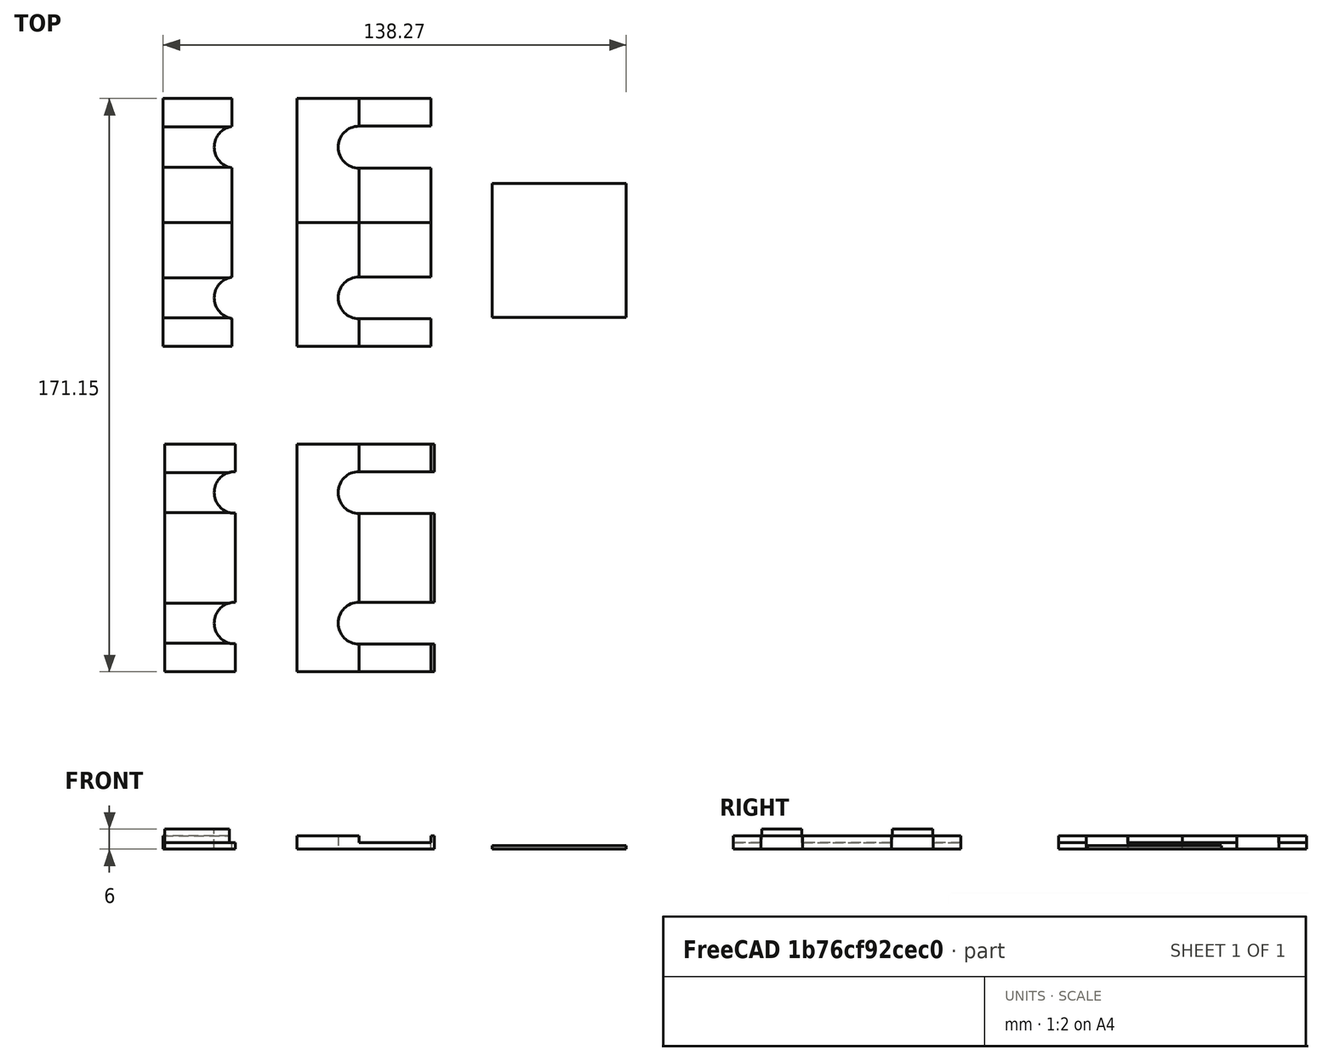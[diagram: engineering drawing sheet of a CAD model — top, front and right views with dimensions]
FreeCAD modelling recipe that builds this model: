
FCSTD DOCUMENT  (FreeCAD 0.20R29177 +426 (Git))
Label: Pipe.Cover
License: All rights reserved
LicenseURL: http://en.wikipedia.org/wiki/All_rights_reserved
objects: Part::Extrusion×30, Part::Part2DObjectPython×20, Part::Feature×19, Part::Cut×12, Part::FeaturePython×10, Part::MultiFuse×9, Part::Refine×5, App::DocumentObjectGroup×5
note: 105 computed .brp shape members not serialized (recipe doc carries the construction recipe); baked Part::Feature solids carry a one-line shape summary decoded from their .brp

FEATURE [Part::Part2DObjectPython] Rectangle  # Draft 2D object (typed FeaturePython)
  Area = 2960
  ChamferSize = 0
  Columns = 1
  FilletRadius = 0
  Height = 74
  Length = 40
  MakeFace = true
  Placement = pos=(-25.3114,-22.2537,0) rot=(0,0,1;0rad)
  Rows = 1
FEATURE [Part::Part2DObjectPython] Circle  # Draft 2D object (typed FeaturePython)
  Area = 122.718
  FirstAngle = 0
  LastAngle = 0
  MakeFace = true
  Placement = pos=(-3.81144,37.2463,0) rot=(0,0,1;0rad)
  Radius = 6.25
FEATURE [Part::Part2DObjectPython] Circle001  # Draft 2D object (typed FeaturePython)
  Area = 122.718
  FirstAngle = 0
  LastAngle = 0
  MakeFace = true
  Placement = pos=(-3.81144,-7.75368,0) rot=(0,0,1;0rad)
  Radius = 6.25
FEATURE [Part::Extrusion] Extrusion
  Base = -> Rectangle
  Dir = (0,0,2)
  DirMode = 0
  FaceMakerClass = Part::FaceMakerBullseye
  LengthFwd = 0
  LengthRev = 0
  Solid = true
  Symmetric = false
FEATURE [Part::Extrusion] Extrusion001
  Base = -> Circle
  Dir = (0,0,27.4704)
  DirMode = 0
  FaceMakerClass = Part::FaceMakerBullseye
  LengthFwd = 0
  LengthRev = 0
  Solid = true
  Symmetric = false
FEATURE [Part::Extrusion] Extrusion002
  Base = -> Circle001
  Dir = (0,0,27.4704)
  DirMode = 0
  FaceMakerClass = Part::FaceMakerBullseye
  LengthFwd = 0
  LengthRev = 0
  Solid = true
  Symmetric = false
FEATURE [Part::Part2DObjectPython] Rectangle002  # Draft 2D object (typed FeaturePython)
  Area = 1040.39
  ChamferSize = 0
  Columns = 1
  FilletRadius = 0
  Height = 83.2313
  Length = 12.5
  MakeFace = true
  Placement = pos=(-87.0428,-14.0037,0) rot=(0.707107,0.707107,0;3.14159rad)
  Rows = 1
FEATURE [Part::Part2DObjectPython] Rectangle003  # Draft 2D object (typed FeaturePython)
  Area = 922.127
  ChamferSize = 0
  Columns = 1
  FilletRadius = 0
  Height = 73.7701
  Length = 12.5
  MakeFace = true
  Placement = pos=(-77.5816,30.9963,0) rot=(0.707107,0.707107,0;3.14159rad)
  Rows = 1
FEATURE [Part::Extrusion] Extrusion003
  Base = -> Rectangle003
  Dir = (0,0,27.4704)
  DirMode = 0
  FaceMakerClass = Part::FaceMakerBullseye
  LengthFwd = 0
  LengthRev = 0
  Solid = true
  Symmetric = false
FEATURE [Part::Extrusion] Extrusion004
  Base = -> Rectangle002
  Dir = (0,0,27.4704)
  DirMode = 0
  FaceMakerClass = Part::FaceMakerBullseye
  LengthFwd = 0
  LengthRev = 0
  Solid = true
  Symmetric = false
FEATURE [Part::Cut] Cut
  Base = -> Extrusion
  Tool = -> Extrusion003
FEATURE [Part::Cut] Cut001
  Base = -> Cut
  Tool = -> Extrusion004
FEATURE [Part::Cut] Cut002
  Base = -> Cut001
  Tool = -> Extrusion001
FEATURE [Part::Cut] Cut003  label="Base"
  Base = -> Cut002
  Tool = -> Extrusion002
FEATURE [Part::Part2DObjectPython] Circle002  # Draft 2D object (typed FeaturePython)
  Area = 122.718
  FirstAngle = 0
  LastAngle = 0
  MakeFace = true
  Placement = pos=(-3.81144,37.2463,0) rot=(0.707107,0.707107,0;3.14159rad)
  Radius = 6.25
FEATURE [Part::Part2DObjectPython] Circle003  # Draft 2D object (typed FeaturePython)
  Area = 122.718
  FirstAngle = 0
  LastAngle = 0
  MakeFace = true
  Placement = pos=(-3.81144,-7.75368,0) rot=(0.707107,0.707107,0;3.14159rad)
  Radius = 6.25
FEATURE [Part::Part2DObjectPython] Rectangle004  # Draft 2D object (typed FeaturePython)
  Area = 268.75
  ChamferSize = 0
  Columns = 1
  FilletRadius = 0
  Height = 21.5
  Length = 12.5
  MakeFace = true
  Placement = pos=(-25.3114,30.9963,0) rot=(0.707107,0.707107,0;3.14159rad)
  Rows = 1
FEATURE [Part::Part2DObjectPython] Rectangle005  # Draft 2D object (typed FeaturePython)
  Area = 268.75
  ChamferSize = 0
  Columns = 1
  FilletRadius = 0
  Height = 21.5
  Length = 12.5
  MakeFace = true
  Placement = pos=(-25.3114,-14.0037,0) rot=(0.707107,0.707107,0;3.14159rad)
  Rows = 1
FEATURE [Part::Extrusion] Extrusion005
  Base = -> Rectangle004
  Dir = (0,0,2)
  DirMode = 0
  FaceMakerClass = Part::FaceMakerBullseye
  LengthFwd = 0
  LengthRev = 0
  Solid = true
  Symmetric = false
FEATURE [Part::Extrusion] Extrusion006
  Base = -> Rectangle005
  Dir = (0,0,2)
  DirMode = 0
  FaceMakerClass = Part::FaceMakerBullseye
  LengthFwd = 0
  LengthRev = 0
  Solid = true
  Symmetric = false
FEATURE [Part::Extrusion] Extrusion007
  Base = -> Circle003
  Dir = (0,0,29.3791)
  DirMode = 0
  FaceMakerClass = Part::FaceMakerBullseye
  LengthFwd = 0
  LengthRev = 0
  Solid = true
  Symmetric = false
FEATURE [Part::Extrusion] Extrusion008
  Base = -> Circle002
  Dir = (0,0,29.3791)
  DirMode = 0
  FaceMakerClass = Part::FaceMakerBullseye
  LengthFwd = 0
  LengthRev = 0
  Solid = true
  Symmetric = false
FEATURE [Part::Cut] Cut004
  Base = -> Extrusion006
  Tool = -> Extrusion007
FEATURE [Part::Cut] Cut005
  Base = -> Extrusion005
  Tool = -> Extrusion008
FEATURE [Part::Feature] Face
  shape: bbox 21.5 x 12.5 x 2e-07 mm, 1 faces, 0 solids (baked)
FEATURE [Part::Extrusion] Extrusion009
  Base = -> Face
  Dir = (0,0,-2)
  DirMode = 0
  FaceMakerClass = Part::FaceMakerBullseye
  LengthFwd = 0
  LengthRev = 0
  Solid = true
  Symmetric = false
FEATURE [Part::Feature] Face001
  shape: bbox 21.5 x 12.5 x 2e-07 mm, 1 faces, 0 solids (baked)
FEATURE [Part::Extrusion] Extrusion010
  Base = -> Face001
  Dir = (0,0,-2)
  DirMode = 0
  FaceMakerClass = Part::FaceMakerBullseye
  LengthFwd = 0
  LengthRev = 0
  Solid = true
  Symmetric = false
FEATURE [Part::Feature] Face002
  shape: bbox 21.5 x 2e-07 x 2 mm, 1 faces, 0 solids (baked)
FEATURE [Part::Extrusion] Extrusion011
  Base = -> Face002
  Dir = (-7.2e-15,-32.5,0)
  DirMode = 0
  FaceMakerClass = Part::FaceMakerBullseye
  LengthFwd = 0
  LengthRev = 0
  Solid = true
  Symmetric = false
FEATURE [Part::Feature] Face003
  shape: bbox 21.5 x 2e-07 x 2 mm, 1 faces, 0 solids (baked)
FEATURE [Part::Extrusion] Extrusion012
  Base = -> Face003
  Dir = (-1.8e-15,-8.25,0)
  DirMode = 0
  FaceMakerClass = Part::FaceMakerBullseye
  LengthFwd = 0
  LengthRev = 0
  Solid = true
  Symmetric = false
FEATURE [Part::Feature] Face004
  shape: bbox 21.5 x 2e-07 x 2 mm, 1 faces, 0 solids (baked)
FEATURE [Part::Extrusion] Extrusion013
  Base = -> Face004
  Dir = (1.8e-15,8.25,0)
  DirMode = 0
  FaceMakerClass = Part::FaceMakerBullseye
  LengthFwd = 0
  LengthRev = 0
  Solid = true
  Symmetric = false
FEATURE [Part::MultiFuse] Fusion
  Shapes = -> [Extrusion013,Extrusion009,Extrusion011,Extrusion010]
FEATURE [Part::MultiFuse] Fusion001
  Shapes = -> [Cut005,Cut004]
FEATURE [Part::MultiFuse] Fusion002  label="cover"
  Shapes = -> [Fusion001,Fusion]
FEATURE [Part::MultiFuse] Fusion003  label="Cover"
  Shapes = -> [Fusion002,Extrusion012]
FEATURE [Part::Feature] Face005
  shape: bbox 40 x 74 x 2e-07 mm, 1 faces, 0 solids (baked)
FEATURE [Part::Extrusion] Extrusion014
  Base = -> Face005
  Dir = (0,0,-2)
  DirMode = 0
  FaceMakerClass = Part::FaceMakerBullseye
  LengthFwd = 0
  LengthRev = 0
  Solid = true
  Symmetric = false
FEATURE [Part::Part2DObjectPython] Rectangle006  # Draft 2D object (typed FeaturePython)
  Area = 1591
  ChamferSize = 0
  Columns = 1
  FilletRadius = 0
  Height = 74
  Length = 21.5
  MakeFace = true
  Placement = pos=(-25.3114,51.7463,-2) rot=(1,0,0;3.14159rad)
  Rows = 1
FEATURE [Part::Extrusion] Extrusion015
  Base = -> Rectangle006
  Dir = (0,0,2)
  DirMode = 0
  FaceMakerClass = Part::FaceMakerBullseye
  LengthFwd = 0
  LengthRev = 0
  Solid = true
  Symmetric = false
FEATURE [Part::Cut] Cut006
  Base = -> Extrusion014
  Tool = -> Extrusion015
FEATURE [Part::MultiFuse] Fusion004
  Shapes = -> [Cut006,Cut003]
FEATURE [Part::Refine] Fusion004001  label="Base001"
  Placement = pos=(29.3771,0,-2e-15) rot=(0,1,0;3.14159rad)
  Source = -> Fusion004
FEATURE [Part::Refine] Fusion003001  label="Cover001"
  Source = -> Fusion003
FEATURE [Part::Feature] Face006
  shape: bbox 2e-07 x 8.25 x 2 mm, 1 faces, 0 solids (baked)
FEATURE [Part::Part2DObjectPython] Rectangle007  # Draft 2D object (typed FeaturePython)
  Area = 1194.48
  ChamferSize = 0
  Columns = 1
  FilletRadius = 0
  Height = 80.4357
  Length = 14.8502
  MakeFace = true
  Placement = pos=(-4.81144,58.182,-2) rot=(1,0,0;3.14159rad)
  Rows = 1
FEATURE [Part::Extrusion] Extrusion016
  Base = -> Rectangle007
  Dir = (0,0,8.60882)
  DirMode = 0
  FaceMakerClass = Part::FaceMakerBullseye
  LengthFwd = 0
  LengthRev = 0
  Solid = true
  Symmetric = false
FEATURE [Part::Cut] Cut007
  Base = -> Fusion003001
  Tool = -> Extrusion016
FEATURE [Part::Feature] Face007
  shape: bbox 20.5 x 3e-07 x 2 mm, 1 faces, 0 solids (baked)
FEATURE [Part::Extrusion] Extrusion017
  Base = -> Face007
  Dir = (1e-16,0.25,0)
  DirMode = 0
  FaceMakerClass = Part::FaceMakerBullseye
  LengthFwd = 0
  LengthRev = 0
  Solid = true
  Symmetric = false
FEATURE [Part::Cut] Cut008
  Base = -> Cut007
  Tool = -> Extrusion017
FEATURE [Part::Feature] Face008
  shape: bbox 20.5 x 3e-07 x 2 mm, 1 faces, 0 solids (baked)
FEATURE [Part::Extrusion] Extrusion018
  Base = -> Face008
  Dir = (-1e-16,-0.25,0)
  DirMode = 0
  FaceMakerClass = Part::FaceMakerBullseye
  LengthFwd = 0
  LengthRev = 0
  Solid = true
  Symmetric = false
FEATURE [Part::Cut] Cut009
  Base = -> Cut008
  Tool = -> Extrusion018
FEATURE [Part::Feature] Face009
  shape: bbox 20.5 x 3e-07 x 2 mm, 1 faces, 0 solids (baked)
FEATURE [Part::Extrusion] Extrusion019
  Base = -> Face009
  Dir = (1e-16,0.25,0)
  DirMode = 0
  FaceMakerClass = Part::FaceMakerBullseye
  LengthFwd = 0
  LengthRev = 0
  Solid = true
  Symmetric = false
FEATURE [Part::Feature] Face010
  shape: bbox 20.5 x 3e-07 x 2 mm, 1 faces, 0 solids (baked)
FEATURE [Part::Extrusion] Extrusion020
  Base = -> Face010
  Dir = (-1e-16,-0.25,0)
  DirMode = 0
  FaceMakerClass = Part::FaceMakerBullseye
  LengthFwd = 0
  LengthRev = 0
  Solid = true
  Symmetric = false
FEATURE [Part::Cut] Cut010
  Base = -> Cut009
  Tool = -> Extrusion020
FEATURE [Part::Cut] Cut011  label="Cover002"
  Base = -> Cut010
  Tool = -> Extrusion019
FEATURE [Part::Part2DObjectPython] Rectangle008  # Draft 2D object (typed FeaturePython)
  Area = 20490.6
  ChamferSize = 0
  Columns = 1
  FilletRadius = 0
  Height = 107.348
  Length = 190.881
  MakeFace = true
  Placement = pos=(-100.252,14.7463,-53.6738) rot=(1,0,0;1.5708rad)
  Rows = 1
FEATURE [Part::Part2DObjectPython] Rectangle009  # Draft 2D object (typed FeaturePython)
  Area = 19454.6
  ChamferSize = 0
  Columns = 1
  FilletRadius = 0
  Height = 93.5657
  Length = 207.925
  MakeFace = true
  Placement = pos=(-64.7917,14.7463,-29.7379) rot=(1,0,0;1.5708rad)
  Rows = 1
FEATURE [Part::FeaturePython] Slice  # WARN: FeaturePython — macro-defined, semantics opaque (R4)
  Base = -> Cut011
  Mode = 1
  Tolerance = 0
  Tools = -> [Rectangle008]
FEATURE [App::DocumentObjectGroup] GrExplode_Slice  label="Exploded Slice"
FEATURE [Part::FeaturePython] Slice001  # WARN: FeaturePython — macro-defined, semantics opaque (R4)
  Base = -> Fusion004001
  Mode = 1
  Tolerance = 0
  Tools = -> [Rectangle009]
FEATURE [App::DocumentObjectGroup] GrExplode_Slice001  label="Exploded Slice001"
FEATURE [Part::Part2DObjectPython] Rectangle010  # Draft 2D object (typed FeaturePython)
  Area = 1600
  ChamferSize = 0
  Columns = 1
  FilletRadius = 0
  Height = 40
  Length = 40
  MakeFace = true
  Placement = pos=(72.9635,26.4369,-2) rot=(1,0,0;3.14159rad)
  Rows = 1
FEATURE [Part::Extrusion] Extrusion021
  Base = -> Rectangle010
  Dir = (0,0,1)
  DirMode = 0
  FaceMakerClass = Part::FaceMakerBullseye
  LengthFwd = 0
  LengthRev = 0
  Solid = true
  Symmetric = false
FEATURE [Part::Refine] Fusion004003001
  Placement = pos=(0,-97.1456,0) rot=(0,0,1;0rad)
FEATURE [Part::MultiFuse] Fusion004003003002
  Placement = pos=(0,-97.1456,0) rot=(0,0,1;0rad)
FEATURE [Part::Part2DObjectPython] Line001  # Draft 2D object (typed FeaturePython)
  Area = 0
  ChamferSize = 0
  Closed = false
  End = (54.6886,-120.399,-2)
  FilletRadius = 0
  Length = 1
  MakeFace = true
  Placement = pos=(54.6886,-119.399,-2) rot=(1,0,0;3.14159rad)
  Points = (2) [(0,0,0),(0,1,0)]
  Start = (54.6886,-119.399,-2)
  Subdivisions = 0
FEATURE [Part::Part2DObjectPython] Rectangle011  # Draft 2D object (typed FeaturePython)
  Area = 6653.61
  ChamferSize = 0
  Columns = 1
  FilletRadius = 0
  Height = 42.255
  Length = 157.463
  MakeFace = true
  Placement = pos=(-82.543,-84.8992,-21.1275) rot=(1,0,0;1.5708rad)
  Rows = 1
FEATURE [Part::Part2DObjectPython] Rectangle012  # Draft 2D object (typed FeaturePython)
  Area = 12333.5
  ChamferSize = 0
  Columns = 1
  FilletRadius = 0
  Height = 102.788
  Length = 119.989
  MakeFace = true
  Placement = pos=(-63.8061,-84.8992,-51.394) rot=(1,0,0;1.5708rad)
  Rows = 1
FEATURE [Part::FeaturePython] Slice002  # WARN: FeaturePython — macro-defined, semantics opaque (R4)
  Base = -> Fusion004003003002
  Mode = 1
  Tolerance = 0
  Tools = -> [Rectangle012]
FEATURE [Part::FeaturePython] Slice002_child0  label="Slice002.0"  # WARN: FeaturePython — macro-defined, semantics opaque (R4)
  Base = -> Slice002
  FilterType = 1
  Invert = false
  OverrideMaxVal = 0
  WindowFrom = 80
  WindowTo = 100
  items = 0
FEATURE [Part::FeaturePython] Slice002_child1  label="Slice002.1"  # WARN: FeaturePython — macro-defined, semantics opaque (R4)
  Base = -> Slice002
  FilterType = 1
  Invert = false
  OverrideMaxVal = 0
  Placement = pos=(0,-1,0) rot=(0,0,1;0rad)
  WindowFrom = 80
  WindowTo = 100
  items = 1
FEATURE [Part::FeaturePython] Slice003  # WARN: FeaturePython — macro-defined, semantics opaque (R4)
  Base = -> Fusion004003001
  Mode = 1
  Tolerance = 0
  Tools = -> [Rectangle011]
FEATURE [Part::FeaturePython] Slice003_child0  label="Slice003.0"  # WARN: FeaturePython — macro-defined, semantics opaque (R4)
  Base = -> Slice003
  FilterType = 1
  Invert = false
  OverrideMaxVal = 0
  WindowFrom = 80
  WindowTo = 100
  items = 0
FEATURE [Part::FeaturePython] Slice003_child1  label="Slice003.1"  # WARN: FeaturePython — macro-defined, semantics opaque (R4)
  Base = -> Slice003
  FilterType = 1
  Invert = false
  OverrideMaxVal = 0
  Placement = pos=(0,-1,0) rot=(0,0,1;0rad)
  WindowFrom = 80
  WindowTo = 100
  items = 1
FEATURE [Part::MultiFuse] Fusion004003003003
  Shapes = -> [Slice003_child1,Slice003_child0]
FEATURE [Part::MultiFuse] Fusion004003003004
  Shapes = -> [Slice002_child1,Slice002_child0]
FEATURE [App::DocumentObjectGroup] GrExplode_Slice002  label="Exploded Slice002"
  Group = -> [Fusion004003003004]
FEATURE [Part::Part2DObjectPython] Line  # Draft 2D object (typed FeaturePython)
  Area = 0
  ChamferSize = 0
  Closed = false
  End = (-25.8114,-119.399,2)
  FilletRadius = 0
  Length = 0.5
  MakeFace = true
  Placement = pos=(-25.3114,-119.399,2) rot=(0,0,1;3.14159rad)
  Points = (2) [(0,0,0),(0.5,0,0)]
  Start = (-25.3114,-119.399,2)
  Subdivisions = 0
FEATURE [Part::Part2DObjectPython] Rectangle013  # Draft 2D object (typed FeaturePython)
  Area = 1867.12
  ChamferSize = 0
  Columns = 1
  FilletRadius = 0
  Height = 16.7459
  Length = 111.497
  MakeFace = true
  Placement = pos=(-24.8114,-40.3344,-6.37293) rot=(0.57735,-0.57735,-0.57735;2.0944rad)
  Rows = 1
FEATURE [Part::FeaturePython] Slice004  # WARN: FeaturePython — macro-defined, semantics opaque (R4)
  Base = -> Fusion004003003004
  Mode = 1
  Tolerance = 0
  Tools = -> [Rectangle013]
FEATURE [Part::FeaturePython] Slice004_child1  label="Slice004.1"  # WARN: FeaturePython — macro-defined, semantics opaque (R4)
  Base = -> Slice004
  FilterType = 1
  Invert = false
  OverrideMaxVal = 0
  WindowFrom = 80
  WindowTo = 100
  items = 1
FEATURE [App::DocumentObjectGroup] GrExplode_Slice004  label="Exploded Slice004"
  Group = -> [Slice004_child1]
FEATURE [Part::Part2DObjectPython] Line002  # Draft 2D object (typed FeaturePython)
  Area = 0
  ChamferSize = 0
  Closed = false
  End = (55.6886,-51.3992,-2)
  FilletRadius = 0
  Length = 1
  MakeFace = true
  Placement = pos=(54.6886,-51.3992,-2) rot=(0,0,1;3.14159rad)
  Points = (2) [(0,0,0),(-1,0,0)]
  Start = (54.6886,-51.3992,-2)
  Subdivisions = 0
FEATURE [Part::Feature] Face011
  shape: bbox 1.039e-06 x 12.75 x 2 mm, 1 faces, 0 solids (baked)
FEATURE [Part::Extrusion] Extrusion022
  Base = -> Face011
  Dir = (1,0,0)
  DirMode = 0
  FaceMakerClass = Part::FaceMakerBullseye
  LengthFwd = 0
  LengthRev = 0
  Solid = true
  Symmetric = false
FEATURE [Part::Feature] Face012
  shape: bbox 1 x 1.039e-06 x 2 mm, 1 faces, 0 solids (baked)
FEATURE [Part::Extrusion] Extrusion023
  Base = -> Face012
  Dir = (0,13.75,-3.1e-15)
  DirMode = 0
  FaceMakerClass = Part::FaceMakerBullseye
  LengthFwd = 0
  LengthRev = 0
  Solid = true
  Symmetric = false
FEATURE [Part::Feature] Face013
  Placement = pos=(29.3771,-103.146,-2e-15) rot=(0,1,0;3.14159rad)
  shape: bbox 9.387e-07 x 8.25 x 2 mm, 1 faces, 0 solids (baked)
FEATURE [Part::Extrusion] Extrusion024
  Base = -> Face013
  Dir = (1,0,0)
  DirMode = 0
  FaceMakerClass = Part::FaceMakerBullseye
  LengthFwd = 0
  LengthRev = 0
  Solid = true
  Symmetric = false
FEATURE [Part::Feature] Face014
  Placement = pos=(29.3771,-97.1456,-2e-15) rot=(0,1,0;3.14159rad)
  shape: bbox 9.387e-07 x 8.25 x 2 mm, 1 faces, 0 solids (baked)
FEATURE [Part::Extrusion] Extrusion025
  Base = -> Face014
  Dir = (1,0,0)
  DirMode = 0
  FaceMakerClass = Part::FaceMakerBullseye
  LengthFwd = 0
  LengthRev = 0
  Solid = true
  Symmetric = false
FEATURE [Part::Feature] Face015
  shape: bbox 1 x 8.25 x 3e-07 mm, 1 faces, 0 solids (baked)
FEATURE [Part::Extrusion] Extrusion026
  Base = -> Face015
  Dir = (0,0,2)
  DirMode = 0
  FaceMakerClass = Part::FaceMakerBullseye
  LengthFwd = 0
  LengthRev = 0
  Solid = true
  Symmetric = false
FEATURE [Part::Feature] Face016
  shape: bbox 1 x 13.75 x 1.039e-06 mm, 1 faces, 0 solids (baked)
FEATURE [Part::Extrusion] Extrusion027
  Base = -> Face016
  Dir = (0,4e-16,2)
  DirMode = 0
  FaceMakerClass = Part::FaceMakerBullseye
  LengthFwd = 0
  LengthRev = 0
  Solid = true
  Symmetric = false
FEATURE [Part::Feature] Face017
  shape: bbox 1 x 12.75 x 1.039e-06 mm, 1 faces, 0 solids (baked)
FEATURE [Part::Extrusion] Extrusion028
  Base = -> Face017
  Dir = (0,0,2)
  DirMode = 0
  FaceMakerClass = Part::FaceMakerBullseye
  LengthFwd = 0
  LengthRev = 0
  Solid = true
  Symmetric = false
FEATURE [Part::Feature] Face018
  shape: bbox 1 x 8.25 x 3e-07 mm, 1 faces, 0 solids (baked)
FEATURE [Part::Extrusion] Extrusion029
  Base = -> Face018
  Dir = (0,0,2)
  DirMode = 0
  FaceMakerClass = Part::FaceMakerBullseye
  LengthFwd = 0
  LengthRev = 0
  Solid = true
  Symmetric = false
FEATURE [Part::MultiFuse] Fusion004003003005
  Shapes = -> [Extrusion026,Extrusion024,Extrusion027,Extrusion023,Extrusion028,Extrusion022,Extrusion029,Extrusion025,Fusion004003003003]
FEATURE [App::DocumentObjectGroup] GrExplode_Slice003  label="Exploded Slice003"
  Group = -> [Fusion004003003005]
FEATURE [Part::Refine] Slice004_child1001  label="Slice004.002"
  Source = -> Slice004_child1
FEATURE [Part::Refine] Fusion004003003005001
  Source = -> Fusion004003003005
